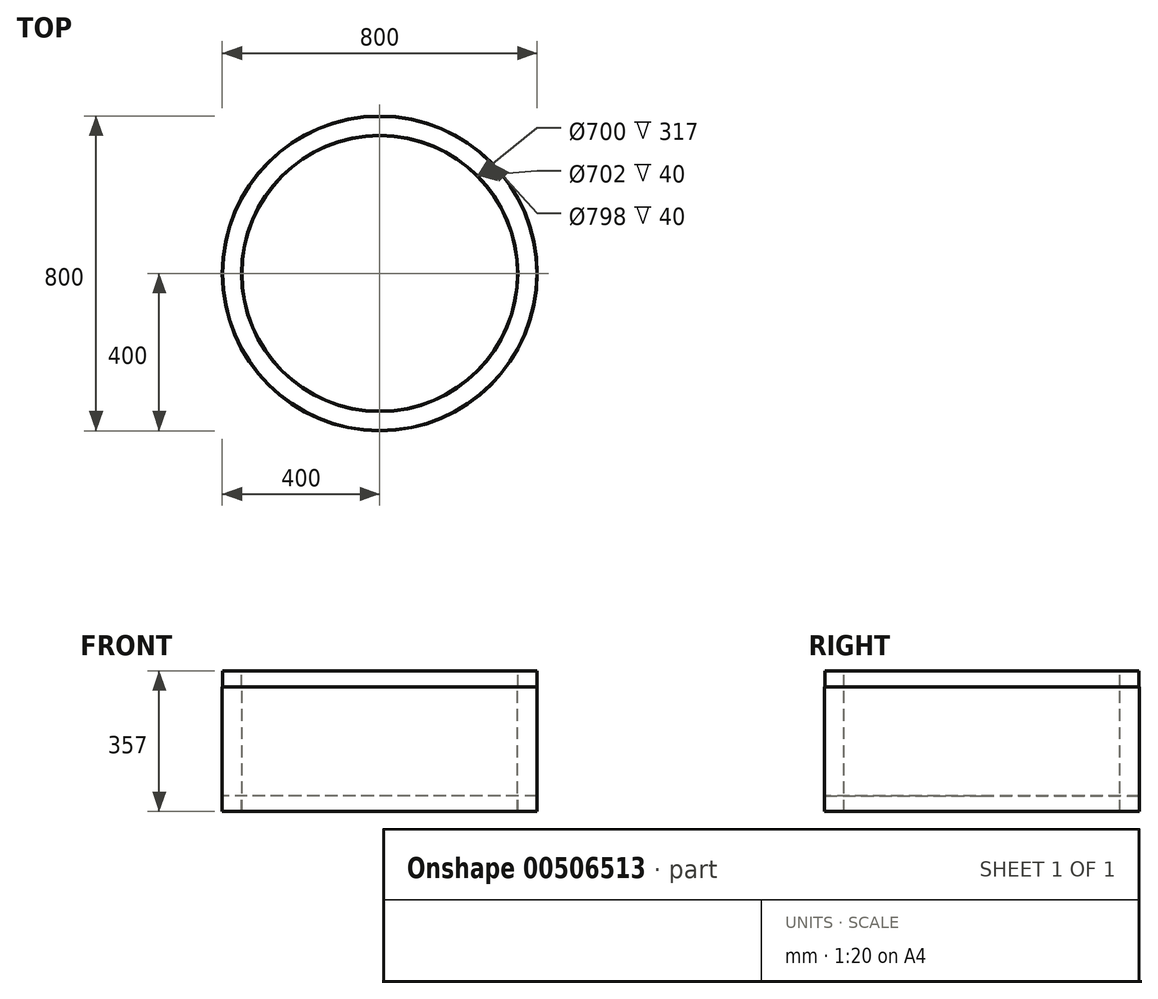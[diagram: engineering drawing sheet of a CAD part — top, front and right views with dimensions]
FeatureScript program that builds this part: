
annotation { "Feature Type Name" : "Feature", "Feature Type Description" : "" }
export const myFeature = defineFeature(function(context is Context, id is Id, definition is map)
    precondition{}
    {
        {
            var Q0;
            Q0=qCreatedBy(makeId("Front.planeOp"),FACE);
            var sketch = newSketch(context, id + "F0", { "sketchPlane" : qUnion([Q0])});
            skLineSegment(sketch, "E0", {"start": v(0, 74.87) * mm, "end": v(0, -73.71) * mm, "construction": true});
            skLineSegment(sketch, "E1", {"start": v(0, 374.84) * mm, "end": v(0, -528.94) * mm, "construction": true});
            skLineSegment(sketch, "E2", {"start": v(-350, -489.75) * mm, "end": v(-350, -172.75) * mm});
            skLineSegment(sketch, "E3", {"start": v(-350, -172.75) * mm, "end": v(-351, -172.75) * mm});
            skLineSegment(sketch, "E4", {"start": v(-351, -172.75) * mm, "end": v(-351, -132.75) * mm});
            skLineSegment(sketch, "E5", {"start": v(-351, -132.75) * mm, "end": v(-399, -132.75) * mm});
            skLineSegment(sketch, "E6", {"start": v(-399, -132.75) * mm, "end": v(-399, -172.75) * mm});
            skLineSegment(sketch, "E7", {"start": v(-399, -172.75) * mm, "end": v(-400, -172.75) * mm});
            skLineSegment(sketch, "E8", {"start": v(-400, -172.75) * mm, "end": v(-400, -489.75) * mm});
            skLineSegment(sketch, "E9", {"start": v(-400, -489.75) * mm, "end": v(-399, -489.75) * mm});
            skLineSegment(sketch, "E10", {"start": v(-399, -489.75) * mm, "end": v(-399, -449.75) * mm});
            skLineSegment(sketch, "E11", {"start": v(-399, -449.75) * mm, "end": v(-351, -449.75) * mm});
            skLineSegment(sketch, "E12", {"start": v(-351, -449.75) * mm, "end": v(-351, -489.75) * mm});
            skLineSegment(sketch, "E13", {"start": v(-351, -489.75) * mm, "end": v(-350, -489.75) * mm});
            skSolve(sketch);
        }
        {
            var Q0;
            Q0=qSketchRegion(id+"F0",true);
            var Q1;
            Q1=sQuery(id+"F0.wireOp",EDGE,"E1");
            revolve(context, id + "F1", {"entities" : qUnion([Q0]), "axis" : qUnion([Q1]), "revolveType" : RevolveType.FULL});
        }
    });
